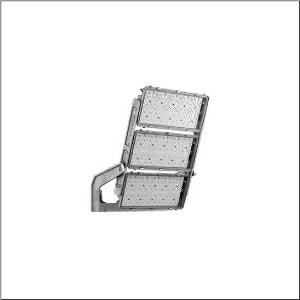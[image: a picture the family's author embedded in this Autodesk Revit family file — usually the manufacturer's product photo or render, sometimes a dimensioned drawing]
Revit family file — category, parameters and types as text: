
# Revit family: floodlight_fl_11_maxi_pro_remote___pl64_5xa779424v01aa_c523
name_source: partatom
category: Lighting Fixtures
units: mm (PartAtom-declared; Revit-internal decimal feet)

## family parameters
Cut with Voids When Loaded = No
Host = Face
Light Source = No
Part Type = Normal
Room Calculation Point = No
Round Connector Dimension = Use Diameter
Shared = No

## types (1)
- --- (1 x LED, 168380 lm, 1539.3 W, 5700K)
    Apparent Load = 1539 VA
    CIE Flux Codes = 28 79 98 100 100
    Color Rendering = 90
    Color Temperature = 5700K
    Default Elevation = 1800 mm
    Description = Floodlight FL 11  maxi  pro Remote floodlight; light control with lens of PMMA; cover panel of toughened safety glass, transparent; light distribution: PL64, asymmetric direct distribution, LEDcolour temperature: 5700K, rated luminous flux: 168.380lm, colour rendering: CRI > 90, light colour: 957; luminous efficacy: 109lm/W; brightness control: DALI 2 (1 DALI address); with terminal, 8-pole, max. 2.5mm², mains connection: 220..240V/380..400V AC, 50/60Hz, surge voltage resistance: line to ground: 10kV, ECG replaceable separately, no afterglow with DALI off / DMX off command, LED unit replaceable without ESD environment, dustproof LED module, dimming range 10..100%; 1539W floodlight with 3x LED unit of diecast aluminium, coated grey; length: 1.003mm / width: 651mm / height: 338mm; mounting bracket, of diecast aluminium, uncoated, natural, equipment: Power, protection rating (complete): IP66; insulation class (complete): insulation class I (protective earthing); certification: CE; ball protection: ball impact resistance with accessories, impact resistance: IK07; only for outdoor installations, rated ambient temperature 10°C, permissible operating ambient temperature: -40..+30°C, permissible storage temperature: -40..+85°Cpackaging unit: 1 piece

Light Distribution: PL64
    Height = 320 mm
    Lamp = 1 x LED
    Lamp Light Flux = 168380 lm
    Lamp Power = 1539.3 W
    Lamp count = 1
    Length = 1002 mm
    Luminous efficacy = 109 lm/W
    Manufacturer = Siteco
    ModVariant = No
    Model = 5XA779424V01AA
    Mounting Place = Ceiling
    Mounting Type = Surface mounted
    Number of Poles = 1
    OnlyDefault = Yes
    Power Factor = 1
    Product Name = Floodlight FL 11 maxi pro Remote | PL64
    Product group = floodlight | ceiling mounted
    ProductGroupID = 301
    Protection Class = Protection class I
    Protection Degree = IP 66
    RLX_Detail_Level = 1
    RLX_Emergency_Light_Flux = 0 lm
    RLX_Emergency_Type = 0
    RLX_Emergency_Type_DB = No
    RlxData = <blob elided: 52485 chars, md5=e77b5541>
    Socket = socket
    Standby Power = 0 W
    System Light Flux = 168380 lm
    System Power = 1539 W
    Type Comments = factory setting: luminous flux: 100 % | dim-lin: 254 | 1080 mA
    Type Image = l_1349141.jpg
    URL = http://relux.com
    VarID = @adj_102480
    Voltage = 0 V
    Weight = 0.00 kg
    Width = 655 mm

## geometry (parser evidence)
native form markers: Blend x4, Sweep x11
no freeform markers — native parametric forms only
